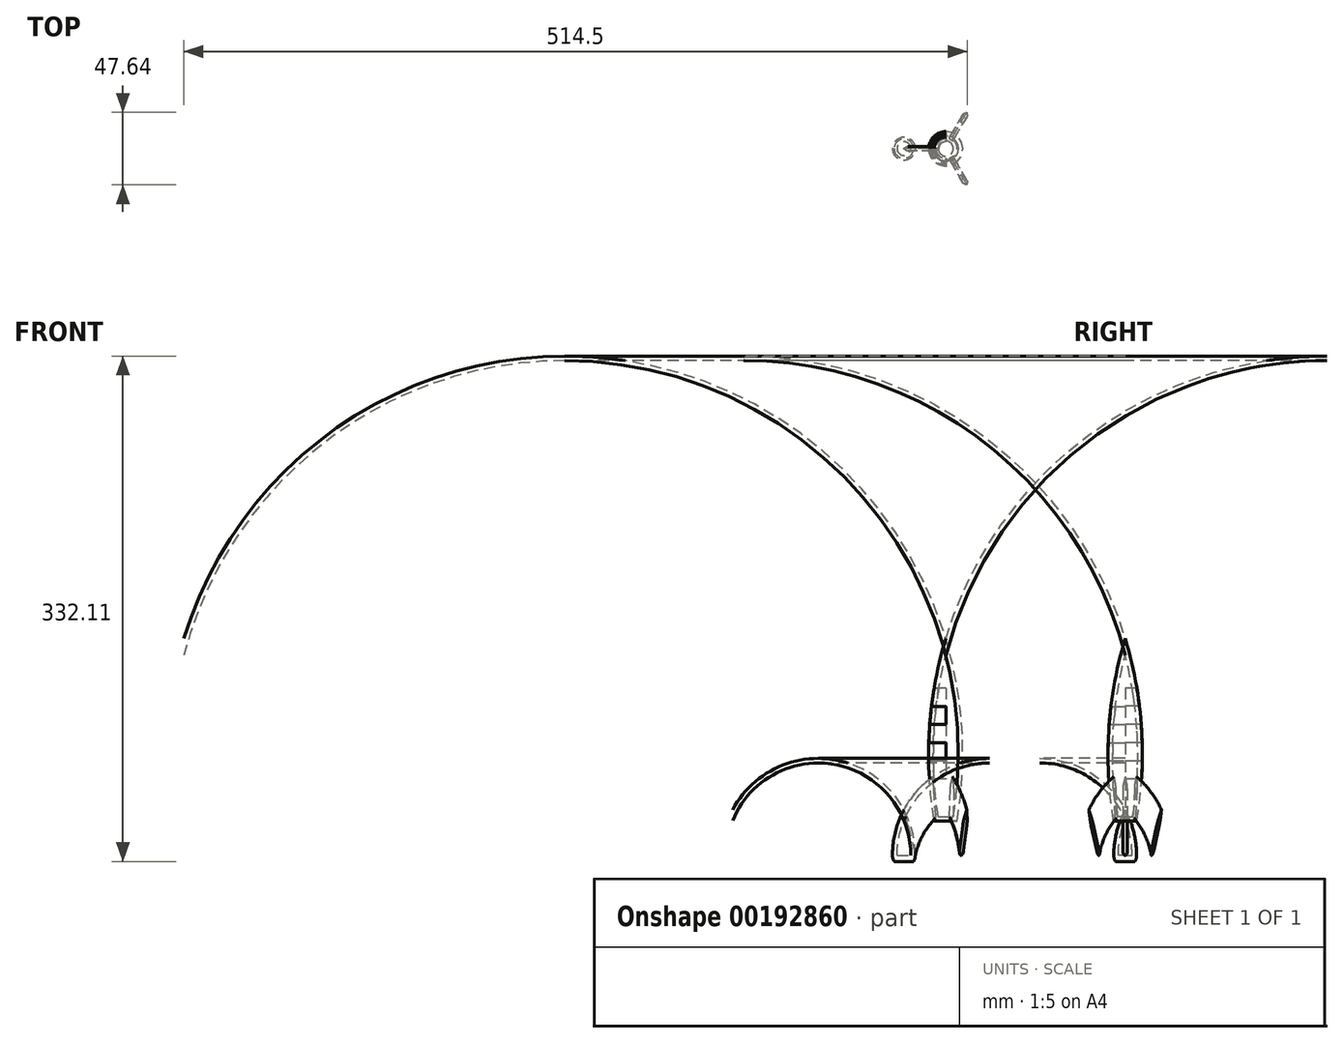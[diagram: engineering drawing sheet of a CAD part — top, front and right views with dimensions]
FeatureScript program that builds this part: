
annotation { "Feature Type Name" : "Feature", "Feature Type Description" : "" }
export const myFeature = defineFeature(function(context is Context, id is Id, definition is map)
    precondition{}
    {
        {
            var Q0;
            Q0=qCreatedBy(makeId("Front.planeOp"),FACE);
            var sketch = newSketch(context, id + "F0", { "sketchPlane" : qUnion([Q0])});
            skArc(sketch, "E0", {"start": v(-35, 0) * mm, "mid": v(-32.8, -5.3) * mm, "end": v(-27.5, -7.5) * mm});
            skArc(sketch, "E1", {"start": v(-27.5, 30) * mm, "mid": v(-33.1, 15.46) * mm, "end": v(-35, 0) * mm});
            skLineSegment(sketch, "E2", {"start": v(-27.5, -7.5) * mm, "end": v(-27.5, -4.5) * mm});
            skArc(sketch, "E3.0", {"start": v(-32, 0) * mm, "mid": v(-30.68, -3.18) * mm, "end": v(-27.5, -4.5) * mm});
            skArc(sketch, "E3.1", {"start": v(-27.5, 22.95) * mm, "mid": v(-30.86, 11.7) * mm, "end": v(-32, 0) * mm});
            skLineSegment(sketch, "E4.trimOffspring", {"start": v(-27.5, 22.95) * mm, "end": v(-27.5, 30) * mm});
            skLineSegment(sketch, "E5", {"start": v(-27.5, -4.5) * mm, "end": v(-27.5, 0) * mm});
            skLineSegment(sketch, "E6", {"start": v(-32, 0) * mm, "end": v(-27.5, 0) * mm});
            skSolve(sketch);
        }
        {
            var Q0;
            Q0 = qSketchRegion(id + "F0", true);
            var Q1;
            Q1=sQuery(id+"F0.wireOp",EDGE,"E2");
            revolve(context, id + "F1", {"surfaceOperationType" : NewSurfaceOperationType.NEW, "entities" : qUnion([Q0]), "axis" : qUnion([Q1]), "revolveType" : RevolveType.FULL});
        }
        {
            var Q0;
            Q0=qCreatedBy(makeId("Front.planeOp"),FACE);
            var sketch = newSketch(context, id + "F2", { "sketchPlane" : qUnion([Q0])});
            skLineSegment(sketch, "E7", {"start": v(0, 22.5) * mm, "end": v(-7.5, 22.5) * mm});
            skArc(sketch, "E8", {"start": v(0, 142.5) * mm, "mid": v(-10.74, 82.94) * mm, "end": v(-7.5, 22.5) * mm});
            skLineSegment(sketch, "E9", {"start": v(0, 22.5) * mm, "end": v(0, 25.5) * mm});
            skLineSegment(sketch, "E10", {"start": v(-11.25, 209.71) * mm, "end": v(-11.25, -89.83) * mm, "construction": true});
            skLineSegment(sketch, "E11.0", {"start": v(0, 25.5) * mm, "end": v(-4.96, 25.5) * mm});
            skArc(sketch, "E11.1", {"start": v(0, 131.4) * mm, "mid": v(-7.97, 78.71) * mm, "end": v(-4.96, 25.5) * mm});
            skLineSegment(sketch, "E12.trimOffspring", {"start": v(0, 131.4) * mm, "end": v(0, 142.5) * mm});
            skSolve(sketch);
        }
        {
            var Q0;
            Q0 = qSketchRegion(id + "F2", true);
            var Q1;
            Q1=sQuery(id+"F2.wireOp",EDGE,"E9");
            revolve(context, id + "F3", {"entities" : qUnion([Q0]), "axis" : qUnion([Q1]), "revolveType" : RevolveType.FULL});
        }
        {
            var Q0;
            Q0=qCreatedBy(makeId("Front.planeOp"),FACE);
            var sketch = newSketch(context, id + "F4", { "sketchPlane" : qUnion([Q0])});
            skArc(sketch, "E13", {"start": v(-8.62, 51.65) * mm, "mid": v(-19.3, 41.9) * mm, "end": v(-27.5, 30) * mm});
            skArc(sketch, "E14", {"start": v(-6.85, 24.46) * mm, "mid": v(-15.2, 13.19) * mm, "end": v(-20, 0) * mm});
            skLineSegment(sketch, "E15", {"start": v(-27.5, 30) * mm, "end": v(-20, 0) * mm});
            skLineSegment(sketch, "E16", {"start": v(-8.62, 51.65) * mm, "end": v(-6.85, 24.46) * mm});
            skPoint(sketch, "E17.start.orphan", {"position": v(0, 56.9) * mm});
            skSolve(sketch);
        }
        {
            var Q0;
            Q0 = qSketchRegion(id + "F4", true);
            extrude(context, id + "F5", {"entities" : qUnion([Q0]), "depth" : 3 * mm, "symmetric" : true});
        }
        {
            var Q0;
            Q0=makeQuery(id+"F5.opExtrude","CAP_EDGE",EDGE,{"disambiguationData":[OSD([sQuery(id+"F4.wireOp",EDGE,"E13")])],"isStart":false});
            var Q1;
            Q1=makeQuery(id+"F5.opExtrude","CAP_EDGE",EDGE,{"disambiguationData":[OSD([sQuery(id+"F4.wireOp",EDGE,"E13")])],"isStart":true});
            chamfer(context, id + "F6", {"entities" : qUnion([Q0, Q1]), "chamferType" : ChamferType.TWO_OFFSETS, "width1" : 5 * mm, "oppositeDirection" : false, "width2" : 1.5 * mm, "tangentPropagation" : true});
        }
        {
            var Q0;
            {var subQ0=sQuery(id+"F4.wireOp",EDGE,"E13");Q0=makeQuery(id+"F6.opChamfer","BLEND_EDGE",EDGE,{"blendedFrom":[makeQuery(id+"F5.opExtrude","CAP_EDGE",EDGE,{"disambiguationData":[OSD([subQ0])],"isStart":false}),makeQuery(id+"F5.opExtrude","CAP_FACE",FACE,{"disambiguationData":[OSD([subQ0,sQuery(id+"F4.wireOp",EDGE,"E14"),sQuery(id+"F4.wireOp",EDGE,"E15"),sQuery(id+"F4.wireOp",EDGE,"E17")])],"isStart":false})],"blendedInto":[makeQuery(id+"F5.opExtrude","CAP_FACE",FACE,{"disambiguationData":[OSD([subQ0,sQuery(id+"F4.wireOp",EDGE,"E14"),sQuery(id+"F4.wireOp",EDGE,"E15"),sQuery(id+"F4.wireOp",EDGE,"E17")])],"isStart":false})]});}
            var Q1;
            {var subQ0=sQuery(id+"F4.wireOp",EDGE,"E13");Q1=makeQuery(id+"F6.opChamfer","BLEND_EDGE",EDGE,{"blendedFrom":[makeQuery(id+"F5.opExtrude","CAP_EDGE",EDGE,{"disambiguationData":[OSD([subQ0])],"isStart":true}),makeQuery(id+"F5.opExtrude","CAP_FACE",FACE,{"disambiguationData":[OSD([subQ0,sQuery(id+"F4.wireOp",EDGE,"E14"),sQuery(id+"F4.wireOp",EDGE,"E15"),sQuery(id+"F4.wireOp",EDGE,"E17")])],"isStart":true})],"blendedInto":[makeQuery(id+"F5.opExtrude","CAP_FACE",FACE,{"disambiguationData":[OSD([subQ0,sQuery(id+"F4.wireOp",EDGE,"E14"),sQuery(id+"F4.wireOp",EDGE,"E15"),sQuery(id+"F4.wireOp",EDGE,"E17")])],"isStart":true})]});}
            fillet(context, id + "F7", {"entities" : qUnion([Q0, Q1]), "radius" : 10 * mm, "tangentPropagation" : true, "allowEdgeOverflow" : false});
        }
        {
            var Q0;
            Q0=makeQuery(id+"F5.opExtrude","CAP_EDGE",EDGE,{"disambiguationData":[OSD([sQuery(id+"F4.wireOp",EDGE,"E14")])],"isStart":false});
            var Q1;
            Q1=makeQuery(id+"F5.opExtrude","CAP_EDGE",EDGE,{"disambiguationData":[OSD([sQuery(id+"F4.wireOp",EDGE,"E14")])],"isStart":true});
            fillet(context, id + "F8", {"entities" : qUnion([Q0, Q1]), "radius" : 1.5 * mm, "tangentPropagation" : true, "allowEdgeOverflow" : false});
        }
        {
            var Q0;
            Q0=makeQuery(id+"F5.opExtrude","SWEPT_BODY",BODY,{"disambiguationData":[OSD([sQuery(id+"F4.wireOp",EDGE,"E13"),sQuery(id+"F4.wireOp",EDGE,"E14"),sQuery(id+"F4.wireOp",EDGE,"E15"),sQuery(id+"F4.wireOp",EDGE,"E17")])]});
            var Q1;
            Q1=sQuery(id+"F2.wireOp",EDGE,"E9");
            circularPattern(context, id + "F9", {"entities" : qUnion([Q0]), "axis" : qUnion([Q1]), "angle" : 360 * degree, "instanceCount" : 3, "equalSpace" : true});
        }
        {
            var Q0;
            Q0=qCreatedBy(makeId("Front.planeOp"),FACE);
            var sketch = newSketch(context, id + "F10", { "sketchPlane" : qUnion([Q0])});
            skArc(sketch, "E18", {"start": v(0, 142.5) * mm, "mid": v(-5.64, 120.48) * mm, "end": v(-9.35, 98.05) * mm});
            skArc(sketch, "E19.0", {"start": v(-4.58, 110.05) * mm, "mid": v(-5.52, 104.06) * mm, "end": v(-6.33, 98.05) * mm});
            skLineSegment(sketch, "E20", {"start": v(-7.62, 110.05) * mm, "end": v(-4.58, 110.05) * mm});
            skLineSegment(sketch, "E21", {"start": v(-9.35, 98.05) * mm, "end": v(-6.33, 98.05) * mm});
            skLineSegment(sketch, "E22", {"start": v(-10.53, 86.05) * mm, "end": v(-7.52, 86.05) * mm});
            skLineSegment(sketch, "E23", {"start": v(-11.14, 74.05) * mm, "end": v(-8.14, 74.05) * mm});
            skLineSegment(sketch, "E24", {"start": v(-11.2, 62.05) * mm, "end": v(-8.2, 62.05) * mm});
            skLineSegment(sketch, "E25", {"start": v(-10.72, 50.05) * mm, "end": v(-7.72, 50.05) * mm});
            skArc(sketch, "E26.trimOffspring", {"start": v(-11.2, 62.05) * mm, "mid": v(-10.1, 42.2) * mm, "end": v(-7.5, 22.5) * mm});
            skArc(sketch, "E27.trimOffspring", {"start": v(-8.2, 62.05) * mm, "mid": v(-8.03, 56.05) * mm, "end": v(-7.72, 50.05) * mm});
            skArc(sketch, "E28.trimOffspring", {"start": v(-10.53, 86.05) * mm, "mid": v(-10.9, 80.05) * mm, "end": v(-11.14, 74.05) * mm});
            skArc(sketch, "E29.trimOffspring", {"start": v(-7.52, 86.05) * mm, "mid": v(-7.9, 80.05) * mm, "end": v(-8.14, 74.05) * mm});
            skSolve(sketch);
        }
        {
            var Q0;
            Q0 = qSketchRegion(id + "F10", true);
            var Q1;
            Q1=sQuery(id+"F2.wireOp",EDGE,"E9");
            revolve(context, id + "F11", {"operationType" : NewBodyOperationType.REMOVE, "entities" : qUnion([Q0]), "axis" : qUnion([Q1]), "revolveType" : RevolveType.ONE_DIRECTION, "oppositeDirection" : true, "angle" : 90 * degree});
        }
        {
            var Q0;
            Q0 = qSketchRegion(id + "F10", true);
            var Q1;
            Q1=sQuery(id+"F2.wireOp",EDGE,"E9");
            revolve(context, id + "F12", {"entities" : qUnion([Q0]), "axis" : qUnion([Q1]), "revolveType" : RevolveType.ONE_DIRECTION, "oppositeDirection" : true, "angle" : 90 * degree});
        }
        {
            var Q0;
            Q0=qCreatedBy(makeId("Front.planeOp"),FACE);
            var sketch = newSketch(context, id + "F13", { "sketchPlane" : qUnion([Q0])});
            skArc(sketch, "E30", {"start": v(0, 142.5) * mm, "mid": v(-6.8, 114.61) * mm, "end": v(-10.52, 86.15) * mm});
            skLineSegment(sketch, "E31", {"start": v(-12.25, 97.95) * mm, "end": v(-4.75, 97.95) * mm});
            skLineSegment(sketch, "E32", {"start": v(-14.03, 86.15) * mm, "end": v(-3.75, 86.15) * mm});
            skLineSegment(sketch, "E33", {"start": v(-14.13, 73.95) * mm, "end": v(-5.73, 73.95) * mm});
            skLineSegment(sketch, "E34", {"start": v(-14.64, 62.15) * mm, "end": v(-4.97, 62.15) * mm});
            skArc(sketch, "E35.0", {"start": v(-6.35, 97.95) * mm, "mid": v(-7, 92.06) * mm, "end": v(-7.51, 86.15) * mm});
            skArc(sketch, "E36.trimOffspring", {"start": v(-8.15, 73.95) * mm, "mid": v(-8.25, 68.05) * mm, "end": v(-8.21, 62.15) * mm});
            skArc(sketch, "E37.trimOffspring", {"start": v(-11.15, 73.95) * mm, "mid": v(-10.6, 48.13) * mm, "end": v(-7.5, 22.5) * mm});
            skSolve(sketch);
        }
        {
            var Q0;
            Q0 = qSketchRegion(id + "F13", true);
            var Q1;
            Q1=sQuery(id+"F2.wireOp",EDGE,"E9");
            revolve(context, id + "F14", {"operationType" : NewBodyOperationType.REMOVE, "entities" : qUnion([Q0]), "axis" : qUnion([Q1]), "revolveType" : RevolveType.ONE_DIRECTION, "angle" : 90 * degree});
        }
        {
            var Q0;
            Q0 = qSketchRegion(id + "F13", true);
            var Q1;
            Q1=sQuery(id+"F2.wireOp",EDGE,"E9");
            revolve(context, id + "F15", {"entities" : qUnion([Q0]), "axis" : qUnion([Q1]), "revolveType" : RevolveType.ONE_DIRECTION, "angle" : 90 * degree});
        }
        {
            var Q0;
            Q0=qCreatedBy(makeId("Top.planeOp"),FACE);
            cPlane(context, id + "F16", {"entities" : qUnion([Q0]), "cplaneType" : CPlaneType.OFFSET, "offset" : 4 * mm, "oppositeDirection" : true, "width" : 150 * mm, "height" : 150 * mm});
        }
        {
            var Q0;
            Q0=qCreatedBy(id+"F16.planeOp",FACE);
            var sketch = newSketch(context, id + "F17", { "sketchPlane" : qUnion([Q0])});
            skLineSegment(sketch, "E38.bottom", {"start": v(-44.71, 37.18) * mm, "end": v(35.75, 37.18) * mm});
            skLineSegment(sketch, "E38.top", {"start": v(-44.71, -39.83) * mm, "end": v(35.75, -39.83) * mm});
            skLineSegment(sketch, "E38.left", {"start": v(-44.71, 37.18) * mm, "end": v(-44.71, -39.83) * mm});
            skLineSegment(sketch, "E38.right", {"start": v(35.75, 37.18) * mm, "end": v(35.75, -39.83) * mm});
            skSolve(sketch);
        }
        {
            var Q0;
            Q0 = qSketchRegion(id + "F17", true);
            extrude(context, id + "F18", {"entities" : qUnion([Q0]), "operationType" : NewBodyOperationType.REMOVE, "oppositeDirection" : true, "depth" : 25 * mm});
        }
    });
